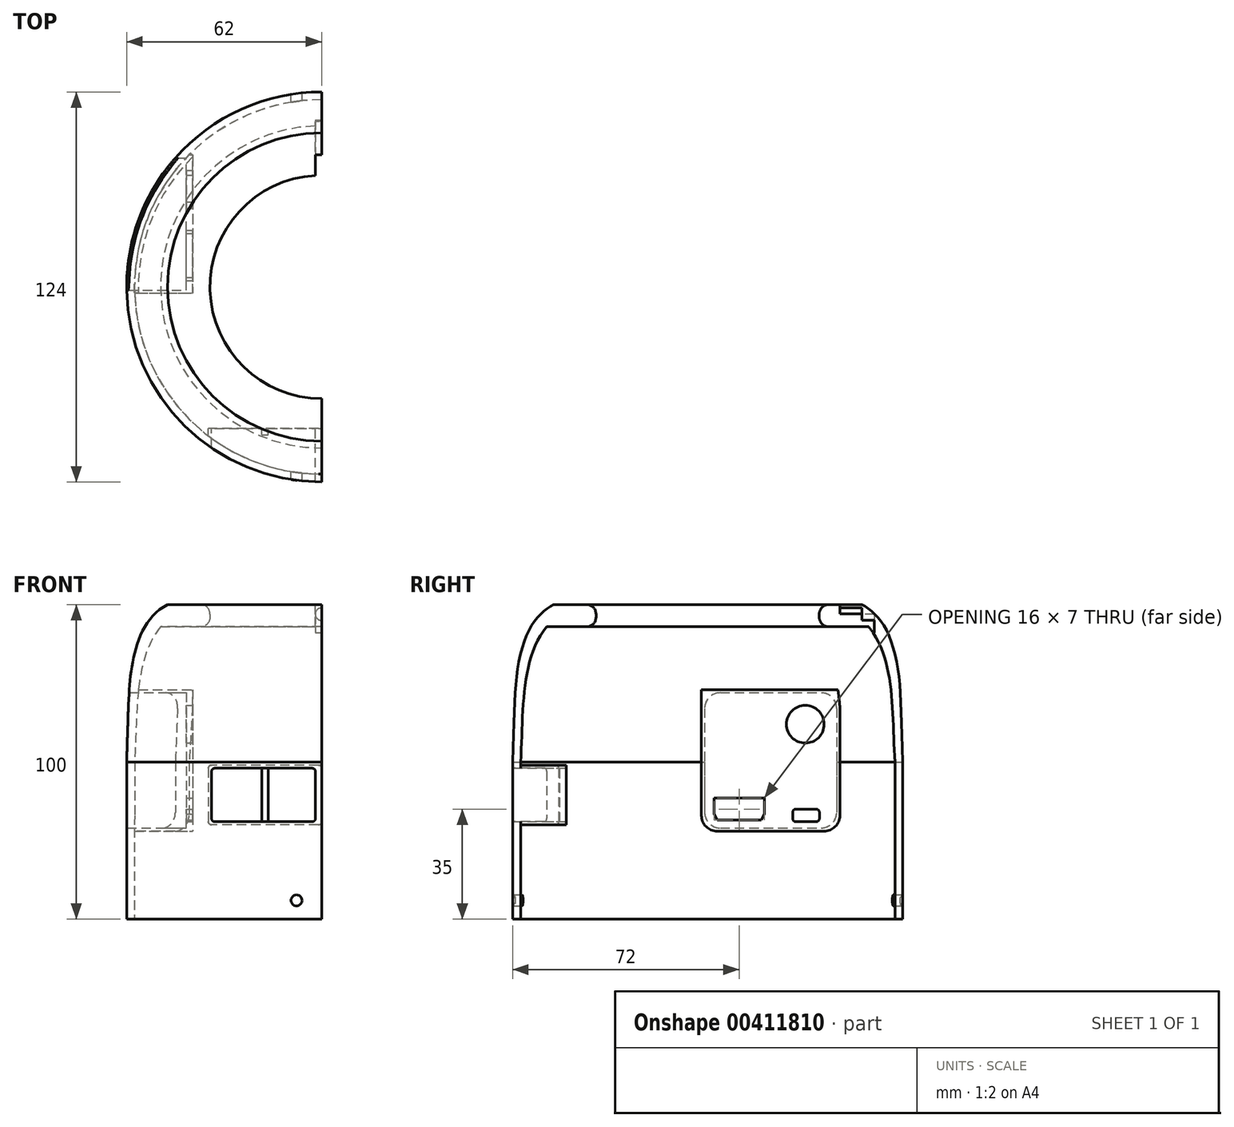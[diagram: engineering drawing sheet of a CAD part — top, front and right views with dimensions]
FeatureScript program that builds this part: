
annotation { "Feature Type Name" : "Feature", "Feature Type Description" : "" }
export const myFeature = defineFeature(function(context is Context, id is Id, definition is map)
    precondition{}
    {
        {
            var Q0;
            Q0=qCreatedBy(makeId("Front.planeOp"),FACE);
            var sketch = newSketch(context, id + "F0", { "sketchPlane" : qUnion([Q0])});
            skLineSegment(sketch, "E0", {"start": v(-38.5, 50) * mm, "end": v(-49, 50) * mm});
            skLineSegment(sketch, "E1", {"start": v(-62, 0) * mm, "end": v(-62, -50) * mm});
            skLineSegment(sketch, "E2", {"start": v(-35.5, 47) * mm, "end": v(-35.5, 46) * mm});
            skLineSegment(sketch, "E3", {"start": v(-38.5, 43) * mm, "end": v(-51.2, 43) * mm});
            skFitSpline(sketch, "E4", {"points": [v(-49, 50) * mm, v(-52.64, 47.47) * mm, v(-56.76, 41.98) * mm, v(-60.39, 29.9) * mm, v(-62, 0) * mm], "startDerivative": vector(-21.37, -10.6) * mm, "endDerivative": vector(-3.86, -109.3) * mm});
            skPoint(sketch, "E5.visualSharp", {"position": v(-35.5, 50) * mm});
            skArc(sketch, "E5.filletArc", {"start": v(-35.5, 47) * mm, "mid": v(-36.38, 49.12) * mm, "end": v(-38.5, 50) * mm});
            skPoint(sketch, "E6.visualSharp", {"position": v(-35.5, 43) * mm});
            skArc(sketch, "E6.filletArc", {"start": v(-38.5, 43) * mm, "mid": v(-36.38, 43.88) * mm, "end": v(-35.5, 46) * mm});
            skLineSegment(sketch, "E7", {"start": v(-62, -50) * mm, "end": v(0, -50) * mm});
            skLineSegment(sketch, "E8", {"start": v(-59.5, -50) * mm, "end": v(-59.5, 0) * mm});
            skFitSpline(sketch, "E9", {"points": [v(-51.2, 43) * mm, v(-59.5, 0) * mm], "startDerivative": vector(-25.81, -31.95) * mm, "endDerivative": vector(-3.04, -46.67) * mm});
            skLineSegment(sketch, "E10", {"start": v(0, -50) * mm, "end": v(0, -45.2) * mm});
            skSolve(sketch);
        }
        {
            var Q0;
            Q0=makeQuery(id+"F0.imprint","IMPRINT",FACE,{"disambiguationData":[TD([[makeQuery(id+"F0.imprint","IMPRINT",EDGE,{"derivedFrom":sQuery(id+"F0.wireOp",EDGE,"E0")}),1.0]])]});
            var Q1;
            Q1=sQuery(id+"F0.wireOp",EDGE,"E10");
            revolve(context, id + "F1", {"entities" : qUnion([Q0]), "axis" : qUnion([Q1]), "revolveType" : RevolveType.SYMMETRIC, "angle" : 180 * degree});
        }
        {
            var Q0;
            Q0=qCreatedBy(makeId("Front.planeOp"),FACE);
            var sketch = newSketch(context, id + "F2", { "sketchPlane" : qUnion([Q0])});
            skCircle(sketch, "E11", {"center": v(0, 47) * mm, "radius": 2 * mm});
            skLineSegment(sketch, "E12", {"start": v(-2, 47.07) * mm, "end": v(-2, 41.07) * mm});
            skLineSegment(sketch, "E13", {"start": v(-2, 41.07) * mm, "end": v(0, 41.07) * mm});
            skLineSegment(sketch, "E14", {"start": v(0, 41.07) * mm, "end": v(0, 45) * mm});
            skLineSegment(sketch, "E15", {"start": v(-2, 47.07) * mm, "end": v(-2, 50.36) * mm});
            skLineSegment(sketch, "E16", {"start": v(0, 50.36) * mm, "end": v(0, 49) * mm});
            skLineSegment(sketch, "E17", {"start": v(-2, 50.36) * mm, "end": v(0, 50.36) * mm});
            skSolve(sketch);
        }
        {
            var Q0;
            {var subQ1=sQuery(id+"F2.wireOp",EDGE,"E11");var subQ4=makeQuery(id+"F2.imprint","INTERSECT",VERTEX,{"derivedFrom":[subQ1,sQuery(id+"F2.wireOp",EDGE,"E14")]});Q0=makeQuery(id+"F2.imprint","IMPRINT",FACE,{"disambiguationData":[TD([[makeQuery(id+"F2.imprint","IMPRINT",EDGE,{"disambiguationData":[TD([[subQ4,1.0]])],"derivedFrom":subQ1}),1.0]])]});}
            extrude(context, id + "F3", {"entities" : qUnion([Q0]), "operationType" : NewBodyOperationType.REMOVE, "oppositeDirection" : true, "depth" : 49 * mm});
        }
        {
            var Q0;
            {var subQ0=sQuery(id+"F2.wireOp",EDGE,"E15");Q0=makeQuery(id+"F2.imprint","IMPRINT",FACE,{"disambiguationData":[TD([[makeQuery(id+"F2.imprint","IMPRINT",EDGE,{"derivedFrom":subQ0}),-1.0]])]});}
            extrude(context, id + "F4", {"entities" : qUnion([Q0]), "operationType" : NewBodyOperationType.REMOVE, "oppositeDirection" : true, "depth" : 42 * mm});
        }
        {
            var Q0;
            {var subQ4=sQuery(id+"F2.wireOp",EDGE,"E13");Q0=makeQuery(id+"F2.imprint","IMPRINT",FACE,{"disambiguationData":[TD([[makeQuery(id+"F2.imprint","IMPRINT",EDGE,{"derivedFrom":subQ4}),1.0]])]});}
            extrude(context, id + "F5", {"entities" : qUnion([Q0]), "operationType" : NewBodyOperationType.REMOVE, "oppositeDirection" : true, "depth" : 53 * mm});
        }
        {
            var Q0;
            Q0=qCreatedBy(makeId("Right.planeOp"),FACE);
            cPlane(context, id + "F6", {"entities" : qUnion([Q0]), "cplaneType" : CPlaneType.OFFSET, "offset" : 41 * mm, "oppositeDirection" : true, "width" : 150 * mm, "height" : 150 * mm});
        }
        {
            var Q0;
            Q0=qCreatedBy(id+"F6.planeOp",FACE);
            var sketch = newSketch(context, id + "F7", { "sketchPlane" : qUnion([Q0])});
            skLineSegment(sketch, "E18.bottom", {"start": v(4, 22) * mm, "end": v(36, 22) * mm});
            skLineSegment(sketch, "E18.top", {"start": v(4, -21) * mm, "end": v(36, -21) * mm});
            skLineSegment(sketch, "E18.left", {"start": v(-1, 17) * mm, "end": v(-1, -16) * mm});
            skLineSegment(sketch, "E18.right", {"start": v(41, 17) * mm, "end": v(41, -16) * mm});
            skPoint(sketch, "E19.visualSharp", {"position": v(-1, 22) * mm});
            skArc(sketch, "E19.filletArc", {"start": v(4, 22) * mm, "mid": v(0.46, 20.54) * mm, "end": v(-1, 17) * mm});
            skPoint(sketch, "E20.visualSharp", {"position": v(41, 22) * mm});
            skArc(sketch, "E20.filletArc", {"start": v(41, 17) * mm, "mid": v(39.54, 20.54) * mm, "end": v(36, 22) * mm});
            skPoint(sketch, "E21.visualSharp", {"position": v(41, -21) * mm});
            skArc(sketch, "E21.filletArc", {"start": v(36, -21) * mm, "mid": v(39.54, -19.54) * mm, "end": v(41, -16) * mm});
            skPoint(sketch, "E22.visualSharp", {"position": v(-1, -21) * mm});
            skArc(sketch, "E22.filletArc", {"start": v(-1, -16) * mm, "mid": v(0.46, -19.54) * mm, "end": v(4, -21) * mm});
            skLineSegment(sketch, "E23", {"start": v(42, 23) * mm, "end": v(42, -17) * mm});
            skLineSegment(sketch, "E24", {"start": v(37, -22) * mm, "end": v(3, -22) * mm});
            skLineSegment(sketch, "E25", {"start": v(42, 23) * mm, "end": v(-2, 23) * mm});
            skLineSegment(sketch, "E26", {"start": v(-2, 23) * mm, "end": v(-2, -17) * mm});
            skPoint(sketch, "E27.visualSharp", {"position": v(-2, 23) * mm});
            skPoint(sketch, "E28.visualSharp", {"position": v(42, 23) * mm});
            skPoint(sketch, "E29.visualSharp", {"position": v(42, -22) * mm});
            skArc(sketch, "E29.filletArc", {"start": v(37, -22) * mm, "mid": v(40.54, -20.54) * mm, "end": v(42, -17) * mm});
            skPoint(sketch, "E30.visualSharp", {"position": v(-2, -22) * mm});
            skArc(sketch, "E30.filletArc", {"start": v(-2, -17) * mm, "mid": v(-0.54, -20.54) * mm, "end": v(3, -22) * mm});
            skSolve(sketch);
        }
        {
            var Q0;
            Q0=makeQuery(id+"F7.imprint","IMPRINT",FACE,{"disambiguationData":[TD([[makeQuery(id+"F7.imprint","IMPRINT",EDGE,{"derivedFrom":sQuery(id+"F7.wireOp",EDGE,"E18.bottom")}),-1.0]])]});
            extrude(context, id + "F8", {"entities" : qUnion([Q0]), "operationType" : NewBodyOperationType.REMOVE, "oppositeDirection" : true, "depth" : 25 * mm});
        }
        {
            var Q0;
            Q0=makeQuery(id+"F7.imprint","IMPRINT",FACE,{"disambiguationData":[TD([[makeQuery(id+"F7.imprint","IMPRINT",EDGE,{"derivedFrom":sQuery(id+"F7.wireOp",EDGE,"E18.bottom")}),1.0]])]});
            var Q1;
            Q1=makeQuery(id+"F1.opRevolve","SWEPT_FACE",FACE,{"disambiguationData":[OSD([sQuery(id+"F0.wireOp",EDGE,"E8")])]});
            extrude(context, id + "F9", {"entities" : qUnion([Q0]), "operationType" : NewBodyOperationType.ADD, "endBound" : BoundingType.UP_TO_SURFACE, "oppositeDirection" : true, "endBoundEntityFace" : qUnion([Q1]), "depth" : 25 * mm});
        }
        {
            var Q0;
            Q0=makeQuery(id+"F7.imprint","IMPRINT",FACE,{"disambiguationData":[TD([[makeQuery(id+"F7.imprint","IMPRINT",EDGE,{"derivedFrom":sQuery(id+"F7.wireOp",EDGE,"E18.bottom")}),-1.0]])]});
            extrude(context, id + "F10", {"entities" : qUnion([Q0]), "operationType" : NewBodyOperationType.ADD, "oppositeDirection" : true, "depth" : 2 * mm});
        }
        {
            var Q0;
            Q0=qCreatedBy(id+"F6.planeOp",FACE);
            var sketch = newSketch(context, id + "F11", { "sketchPlane" : qUnion([Q0])});
            skLineSegment(sketch, "E31.bottom", {"start": v(28, -15) * mm, "end": v(34.5, -15) * mm});
            skLineSegment(sketch, "E31.top", {"start": v(28, -19) * mm, "end": v(34.5, -19) * mm});
            skLineSegment(sketch, "E31.left", {"start": v(27, -16) * mm, "end": v(27, -18) * mm});
            skLineSegment(sketch, "E31.right", {"start": v(35.5, -16) * mm, "end": v(35.5, -18) * mm});
            skLineSegment(sketch, "E32.bottom", {"start": v(2, -11.5) * mm, "end": v(18, -11.5) * mm});
            skLineSegment(sketch, "E32.top", {"start": v(2, -16.5) * mm, "end": v(18, -16.5) * mm});
            skLineSegment(sketch, "E32.left", {"start": v(2, -11.5) * mm, "end": v(2, -16.5) * mm});
            skLineSegment(sketch, "E32.right", {"start": v(18, -11.5) * mm, "end": v(18, -16.5) * mm});
            skLineSegment(sketch, "E33.bottom", {"start": v(3, -11.5) * mm, "end": v(17, -11.5) * mm});
            skLineSegment(sketch, "E33.top", {"start": v(3, -18.5) * mm, "end": v(17, -18.5) * mm});
            skLineSegment(sketch, "E33.left", {"start": v(3, -18.5) * mm, "end": v(3, -11.5) * mm});
            skLineSegment(sketch, "E33.right", {"start": v(17, -18.5) * mm, "end": v(17, -11.5) * mm});
            skLineSegment(sketch, "E34", {"start": v(17, -18.5) * mm, "end": v(18, -16.5) * mm});
            skLineSegment(sketch, "E35", {"start": v(2, -16.5) * mm, "end": v(3, -18.5) * mm});
            skPoint(sketch, "E36.visualSharp", {"position": v(27, -15) * mm});
            skArc(sketch, "E36.filletArc", {"start": v(28, -15) * mm, "mid": v(27.3, -15.3) * mm, "end": v(27, -16) * mm});
            skPoint(sketch, "E37.visualSharp", {"position": v(35.5, -15) * mm});
            skArc(sketch, "E37.filletArc", {"start": v(35.5, -16) * mm, "mid": v(35.2, -15.3) * mm, "end": v(34.5, -15) * mm});
            skPoint(sketch, "E38.visualSharp", {"position": v(35.5, -19) * mm});
            skArc(sketch, "E38.filletArc", {"start": v(34.5, -19) * mm, "mid": v(35.2, -18.7) * mm, "end": v(35.5, -18) * mm});
            skPoint(sketch, "E39.visualSharp", {"position": v(27, -19) * mm});
            skArc(sketch, "E39.filletArc", {"start": v(27, -18) * mm, "mid": v(27.3, -18.7) * mm, "end": v(28, -19) * mm});
            skCircle(sketch, "E40", {"center": v(31, 12) * mm, "radius": 6 * mm});
            skSolve(sketch);
        }
        {
            var Q0;
            Q0=qSketchRegion(id+"F11",true);
            extrude(context, id + "F12", {"entities" : qUnion([Q0]), "operationType" : NewBodyOperationType.REMOVE, "oppositeDirection" : true, "depth" : 2 * mm});
        }
        {
            var Q0;
            Q0=qCreatedBy(makeId("Front.planeOp"),FACE);
            cPlane(context, id + "F13", {"entities" : qUnion([Q0]), "cplaneType" : CPlaneType.OFFSET, "offset" : 45 * mm, "width" : 150 * mm, "height" : 150 * mm});
        }
        {
            var Q0;
            Q0=qCreatedBy(id+"F13.planeOp",FACE);
            var sketch = newSketch(context, id + "F14", { "sketchPlane" : qUnion([Q0])});
            skLineSegment(sketch, "E41.bottom", {"start": v(-1, -1) * mm, "end": v(-35, -1) * mm});
            skLineSegment(sketch, "E41.top", {"start": v(-1, -20) * mm, "end": v(-35, -20) * mm});
            skLineSegment(sketch, "E41.left", {"start": v(0, -2) * mm, "end": v(0, -19) * mm});
            skLineSegment(sketch, "E41.right", {"start": v(-36, -2) * mm, "end": v(-36, -19) * mm});
            skPoint(sketch, "E42.visualSharp", {"position": v(0, -1) * mm});
            skArc(sketch, "E42.filletArc", {"start": v(0, -2) * mm, "mid": v(-0.3, -1.3) * mm, "end": v(-1, -1) * mm});
            skPoint(sketch, "E43.visualSharp", {"position": v(-36, -20) * mm});
            skArc(sketch, "E43.filletArc", {"start": v(-36, -19) * mm, "mid": v(-35.7, -19.7) * mm, "end": v(-35, -20) * mm});
            skPoint(sketch, "E44.visualSharp", {"position": v(0, -20) * mm});
            skArc(sketch, "E44.filletArc", {"start": v(-1, -20) * mm, "mid": v(-0.3, -19.7) * mm, "end": v(0, -19) * mm});
            skPoint(sketch, "E45.visualSharp", {"position": v(-36, -1) * mm});
            skArc(sketch, "E45.filletArc", {"start": v(-35, -1) * mm, "mid": v(-35.7, -1.3) * mm, "end": v(-36, -2) * mm});
            skLineSegment(sketch, "E46.bottom", {"start": v(-34, -2) * mm, "end": v(-3, -2) * mm});
            skLineSegment(sketch, "E46.top", {"start": v(-34, -19) * mm, "end": v(-3, -19) * mm});
            skLineSegment(sketch, "E46.left", {"start": v(-35, -3) * mm, "end": v(-35, -18) * mm});
            skLineSegment(sketch, "E46.right", {"start": v(-2, -3) * mm, "end": v(-2, -18) * mm});
            skArc(sketch, "E47.filletArc", {"start": v(-34, -2) * mm, "mid": v(-34.7, -2.3) * mm, "end": v(-35, -3) * mm});
            skArc(sketch, "E48.filletArc", {"start": v(-3, -19) * mm, "mid": v(-2.3, -18.7) * mm, "end": v(-2, -18) * mm});
            skArc(sketch, "E49.filletArc", {"start": v(-35, -18) * mm, "mid": v(-34.7, -18.7) * mm, "end": v(-34, -19) * mm});
            skPoint(sketch, "E50.visualSharp", {"position": v(-2, -2) * mm});
            skArc(sketch, "E50.filletArc", {"start": v(-2, -3) * mm, "mid": v(-2.3, -2.3) * mm, "end": v(-3, -2) * mm});
            skLineSegment(sketch, "E51", {"start": v(-19, -19) * mm, "end": v(-19, -2) * mm});
            skLineSegment(sketch, "E52", {"start": v(-17, -2) * mm, "end": v(-17, -19) * mm});
            skSolve(sketch);
        }
        {
            var Q0;
            {var subQ0=sQuery(id+"F14.wireOp",EDGE,"E51");Q0=makeQuery(id+"F14.imprint","IMPRINT",FACE,{"disambiguationData":[TD([[makeQuery(id+"F14.imprint","IMPRINT",EDGE,{"derivedFrom":subQ0}),-1.0]])]});}
            var Q1;
            Q1=makeQuery(id+"F14.imprint","IMPRINT",FACE,{"disambiguationData":[TD([[makeQuery(id+"F14.imprint","IMPRINT",EDGE,{"derivedFrom":sQuery(id+"F14.wireOp",EDGE,"E46.left")}),1.0]])]});
            var Q2;
            Q2=makeQuery(id+"F14.imprint","IMPRINT",FACE,{"disambiguationData":[TD([[makeQuery(id+"F14.imprint","IMPRINT",EDGE,{"derivedFrom":sQuery(id+"F14.wireOp",EDGE,"E46.right")}),-1.0]])]});
            var Q3;
            Q3=makeQuery(id+"F1.opRevolve","SWEPT_FACE",FACE,{"disambiguationData":[OSD([sQuery(id+"F0.wireOp",EDGE,"E1")])]});
            extrude(context, id + "F15", {"entities" : qUnion([Q0, Q1, Q2]), "operationType" : NewBodyOperationType.REMOVE, "endBound" : BoundingType.UP_TO_SURFACE, "endBoundEntityFace" : qUnion([Q3]), "depth" : 25 * mm});
        }
        {
            var Q0;
            Q0=makeQuery(id+"F14.imprint","IMPRINT",FACE,{"disambiguationData":[TD([[makeQuery(id+"F14.imprint","IMPRINT",EDGE,{"derivedFrom":sQuery(id+"F14.wireOp",EDGE,"E41.bottom")}),1.0]])]});
            var Q1;
            Q1=makeQuery(id+"F1.opRevolve","SWEPT_FACE",FACE,{"disambiguationData":[OSD([sQuery(id+"F0.wireOp",EDGE,"E1")])]});
            extrude(context, id + "F16", {"entities" : qUnion([Q0]), "operationType" : NewBodyOperationType.ADD, "endBound" : BoundingType.UP_TO_SURFACE, "endBoundEntityFace" : qUnion([Q1]), "depth" : 25 * mm});
        }
        {
            var Q0;
            {var subQ0=sQuery(id+"F14.wireOp",EDGE,"E51");Q0=makeQuery(id+"F14.imprint","IMPRINT",FACE,{"disambiguationData":[TD([[makeQuery(id+"F14.imprint","IMPRINT",EDGE,{"derivedFrom":subQ0}),-1.0]])]});}
            extrude(context, id + "F17", {"entities" : qUnion([Q0]), "operationType" : NewBodyOperationType.ADD, "depth" : 2 * mm});
        }
        {
            var Q0;
            Q0=qCreatedBy(makeId("Front.planeOp"),FACE);
            var sketch = newSketch(context, id + "F18", { "sketchPlane" : qUnion([Q0])});
            skCircle(sketch, "E53", {"center": v(-8, -44) * mm, "radius": 1.75 * mm});
            skSolve(sketch);
        }
        {
            var Q0;
            Q0=makeQuery(id+"F18.imprint","IMPRINT",FACE,{"disambiguationData":[TD([[makeQuery(id+"F18.imprint","IMPRINT",EDGE,{"derivedFrom":sQuery(id+"F18.wireOp",EDGE,"E53")}),1.0]])]});
            var Q1;
            Q1=sQuery(id+"F18.wireOp",EDGE,"E53");
            extrude(context, id + "F19", {"entities" : qUnion([Q0]), "operationType" : NewBodyOperationType.REMOVE, "surfaceEntities" : qUnion([Q1]), "depth" : 125 * mm, "symmetric" : true});
        }
    });
